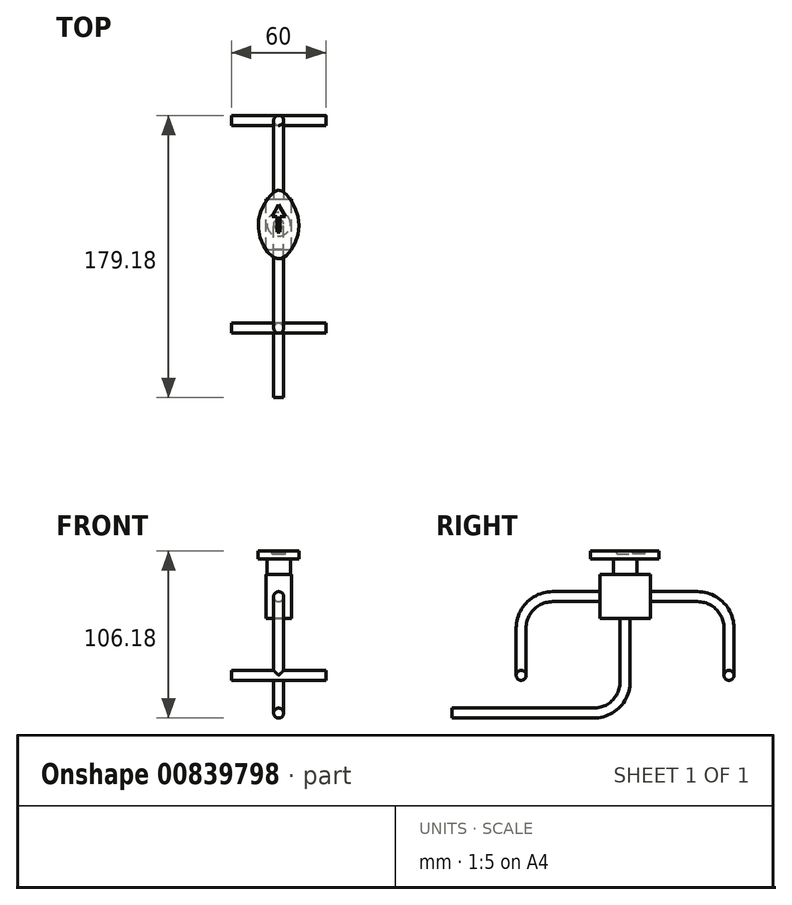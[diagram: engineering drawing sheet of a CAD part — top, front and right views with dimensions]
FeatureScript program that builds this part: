
annotation { "Feature Type Name" : "Feature", "Feature Type Description" : "" }
export const myFeature = defineFeature(function(context is Context, id is Id, definition is map)
    precondition{}
    {
        {
            var Q0;
            Q0=qCreatedBy(makeId("Front.planeOp"),FACE);
            var sketch = newSketch(context, id + "F0", { "sketchPlane" : qUnion([Q0])});
            skLineSegment(sketch, "E0.bottom", {"start": v(-64.04, 98.56) * mm, "end": v(-48.04, 98.56) * mm});
            skLineSegment(sketch, "E0.top", {"start": v(-64.04, 70.56) * mm, "end": v(-48.04, 70.56) * mm});
            skLineSegment(sketch, "E0.left", {"start": v(-64.04, 98.56) * mm, "end": v(-64.04, 70.56) * mm});
            skLineSegment(sketch, "E0.right", {"start": v(-48.04, 98.56) * mm, "end": v(-48.04, 70.56) * mm});
            skLineSegment(sketch, "E1", {"start": v(-56.04, 70.56) * mm, "end": v(-56.04, 30.56) * mm});
            skSolve(sketch);
        }
        {
            var Q0;
            Q0=makeQuery(id+"F0.imprint","IMPRINT",FACE,{"disambiguationData":[TD([[makeQuery(id+"F0.imprint","IMPRINT",EDGE,{"derivedFrom":sQuery(id+"F0.wireOp",EDGE,"E0.bottom")}),-1.0]])]});
            extrude(context, id + "F1", {"entities" : qUnion([Q0]), "endBound" : BoundingType.SYMMETRIC, "depth" : 32 * mm, "offsetDistance" : 25 * mm});
        }
        {
            var Q0;
            Q0=sQuery(id+"F0.wireOp",EDGE,"E1");
            cPlane(context, id + "F2", {"entities" : qUnion([Q0]), "cplaneType" : CPlaneType.LINE_ANGLE, "offset" : 25 * mm, "angle" : 0 * degree, "width" : 150 * mm, "height" : 150 * mm});
        }
        {
            var Q0;
            Q0=qCreatedBy(id+"F2.planeOp",FACE);
            var sketch = newSketch(context, id + "F3", { "sketchPlane" : qUnion([Q0])});
            skLineSegment(sketch, "E2", {"start": v(0, 30.56) * mm, "end": v(40, 30.56) * mm, "construction": true});
            skArc(sketch, "E3", {"start": v(0, 30.56) * mm, "mid": v(5.86, 16.41) * mm, "end": v(20, 10.56) * mm});
            skLineSegment(sketch, "E4", {"start": v(20, 10.56) * mm, "end": v(110, 10.56) * mm});
            skSolve(sketch);
        }
        {
            var Q0;
            Q0=sQuery(id+"F3.wireOp",VERTEX,"E4.end");
            var Q1;
            Q1=sQuery(id+"F3.wireOp",EDGE,"E4");
            cPlane(context, id + "F4", {"entities" : qUnion([Q0, Q1]), "cplaneType" : CPlaneType.CURVE_POINT, "offset" : 25 * mm, "width" : 150 * mm, "height" : 150 * mm});
        }
        {
            var Q0;
            Q0=qCreatedBy(id+"F4.planeOp",FACE);
            var sketch = newSketch(context, id + "F5", { "sketchPlane" : qUnion([Q0])});
            skCircle(sketch, "E5", {"center": v(-56.04, 10.56) * mm, "radius": 3.17 * mm});
            skSolve(sketch);
        }
        {
            var Q0;
            Q0=makeQuery(id+"F5.imprint","IMPRINT",FACE,{"disambiguationData":[TD([[makeQuery(id+"F5.imprint","IMPRINT",EDGE,{"derivedFrom":sQuery(id+"F5.wireOp",EDGE,"E5")}),1.0]])]});
            var Q1;
            Q1=sQuery(id+"F3.wireOp",EDGE,"E4");
            var Q2;
            Q2=sQuery(id+"F3.wireOp",EDGE,"E3");
            var Q3;
            Q3=sQuery(id+"F0.wireOp",EDGE,"E1");
            sweep(context, id + "F6", {"operationType" : NewBodyOperationType.ADD, "profiles" : qUnion([Q0]), "path" : qUnion([Q1, Q2, Q3])});
        }
        {
            var Q0;
            Q0=makeQuery(id+"F1.opExtrude","SWEPT_FACE",FACE,{"disambiguationData":[OSD([sQuery(id+"F0.wireOp",EDGE,"E0.bottom")])]});
            var sketch = newSketch(context, id + "F7", { "sketchPlane" : qUnion([Q0])});
            skLineSegment(sketch, "E6", {"start": v(-56.04, -16) * mm, "end": v(-56.04, 16) * mm, "construction": true});
            skCircle(sketch, "E7", {"center": v(-56.04, 0) * mm, "radius": 7.5 * mm});
            skSolve(sketch);
        }
        {
            var Q0;
            Q0 = qSketchRegion(id + "F7", true);
            extrude(context, id + "F8", {"entities" : qUnion([Q0]), "operationType" : NewBodyOperationType.ADD, "depth" : 10 * mm, "offsetDistance" : 25 * mm});
        }
        {
            var Q0;
            Q0=makeQuery(id+"F8.opExtrude","CAP_FACE",FACE,{"disambiguationData":[OSD([sQuery(id+"F7.wireOp",EDGE,"E7")])],"isStart":false});
            var sketch = newSketch(context, id + "F9", { "sketchPlane" : qUnion([Q0])});
            skLineSegment(sketch, "E8.bottom", {"start": v(-69.04, 20.5) * mm, "end": v(-43.04, 20.5) * mm, "construction": true});
            skLineSegment(sketch, "E8.top", {"start": v(-69.04, -20.5) * mm, "end": v(-43.04, -20.5) * mm, "construction": true});
            skLineSegment(sketch, "E8.left", {"start": v(-69.04, 20.5) * mm, "end": v(-69.04, -20.5) * mm, "construction": true});
            skLineSegment(sketch, "E8.right", {"start": v(-43.04, 20.5) * mm, "end": v(-43.04, -20.5) * mm, "construction": true});
            skPoint(sketch, "E8.middle", {"position": v(-56.04, 0) * mm});
            skFitSpline(sketch, "E9", {"points": [v(-59.04, 20.5) * mm, v(-69.04, 0) * mm, v(-60.04, -20.5) * mm, v(-52.04, -20.5) * mm, v(-43.04, 0) * mm, v(-53.04, 20.5) * mm, v(-59.04, 20.5) * mm]});
            skSolve(sketch);
        }
        {
            var Q0;
            Q0=makeQuery(id+"F9.imprint","IMPRINT",FACE,{"disambiguationData":[TD([[makeQuery(id+"F9.imprint","IMPRINT",EDGE,{"derivedFrom":sQuery(id+"F9.wireOp",EDGE,"E9")}),1.0]])]});
            var Q1;
            Q1=makeQuery(id+"F9.imprint","IMPRINT",FACE,{"disambiguationData":[TD([[makeQuery(id+"F9.imprint","IMPRINT",EDGE,{"derivedFrom":makeQuery(id+"F8.opExtrude","CAP_EDGE",EDGE,{"disambiguationData":[OSD([sQuery(id+"F7.wireOp",EDGE,"E7")])],"isStart":false})}),1.0]])]});
            extrude(context, id + "F10", {"entities" : qUnion([Q0, Q1]), "operationType" : NewBodyOperationType.ADD, "depth" : 5 * mm, "offsetDistance" : 25 * mm});
        }
        {
            var Q0;
            Q0=makeQuery(id+"F1.opExtrude","CAP_FACE",FACE,{"disambiguationData":[OSD([sQuery(id+"F0.wireOp",EDGE,"E0.bottom"),sQuery(id+"F0.wireOp",EDGE,"E0.top"),sQuery(id+"F0.wireOp",EDGE,"E0.left"),sQuery(id+"F0.wireOp",EDGE,"E0.right")])],"isStart":false});
            var sketch = newSketch(context, id + "F11", { "sketchPlane" : qUnion([Q0])});
            skLineSegment(sketch, "E10", {"start": v(-56.04, 70.56) * mm, "end": v(-56.04, 98.56) * mm, "construction": true});
            skSolve(sketch);
        }
        {
            var Q0;
            Q0=sQuery(id+"F11.wireOp",EDGE,"E10");
            cPlane(context, id + "F12", {"entities" : qUnion([Q0]), "cplaneType" : CPlaneType.LINE_ANGLE, "offset" : 25 * mm, "angle" : 0 * degree, "width" : 150 * mm, "height" : 150 * mm});
        }
        {
            var Q0;
            Q0=qCreatedBy(id+"F12.planeOp",FACE);
            var sketch = newSketch(context, id + "F13", { "sketchPlane" : qUnion([Q0])});
            skLineSegment(sketch, "E11", {"start": v(-16, 84.56) * mm, "end": v(-46, 84.56) * mm});
            skLineSegment(sketch, "E12", {"start": v(-46, 84.56) * mm, "end": v(-46, 44.56) * mm, "construction": true});
            skArc(sketch, "E13", {"start": v(-46, 84.56) * mm, "mid": v(-60.14, 78.7) * mm, "end": v(-66, 64.56) * mm});
            skLineSegment(sketch, "E14", {"start": v(-66, 64.56) * mm, "end": v(-66, 34.56) * mm});
            skSolve(sketch);
        }
        {
            var Q0;
            Q0=sQuery(id+"F13.wireOp",EDGE,"E14");
            cPlane(context, id + "F14", {"entities" : qUnion([Q0]), "cplaneType" : CPlaneType.LINE_ANGLE, "offset" : 25 * mm, "angle" : 270 * degree, "width" : 150 * mm, "height" : 150 * mm});
        }
        {
            var Q0;
            Q0=qCreatedBy(id+"F14.planeOp",FACE);
            var sketch = newSketch(context, id + "F15", { "sketchPlane" : qUnion([Q0])});
            skPoint(sketch, "E15", {"position": v(-56.04, 34.56) * mm});
            skLineSegment(sketch, "E16", {"start": v(-56.04, 34.56) * mm, "end": v(-26.04, 34.56) * mm});
            skSolve(sketch);
        }
        {
            var Q0;
            Q0=sQuery(id+"F15.wireOp",VERTEX,"E16.end");
            var Q1;
            Q1=sQuery(id+"F15.wireOp",EDGE,"E16");
            cPlane(context, id + "F16", {"entities" : qUnion([Q0, Q1]), "cplaneType" : CPlaneType.CURVE_POINT, "offset" : 25 * mm, "width" : 150 * mm, "height" : 150 * mm});
        }
        {
            var Q0;
            Q0=qCreatedBy(id+"F16.planeOp",FACE);
            var sketch = newSketch(context, id + "F17", { "sketchPlane" : qUnion([Q0])});
            skCircle(sketch, "E17", {"center": v(-66, 34.56) * mm, "radius": 3.17 * mm});
            skSolve(sketch);
        }
        {
            var Q0;
            Q0=makeQuery(id+"F17.imprint","IMPRINT",FACE,{"disambiguationData":[TD([[makeQuery(id+"F17.imprint","IMPRINT",EDGE,{"derivedFrom":sQuery(id+"F17.wireOp",EDGE,"E17")}),1.0]])]});
            var Q1;
            Q1=sQuery(id+"F15.wireOp",EDGE,"E16");
            var Q2;
            Q2=sQuery(id+"F13.wireOp",EDGE,"E14");
            var Q3;
            Q3=sQuery(id+"F13.wireOp",EDGE,"E13");
            var Q4;
            Q4=sQuery(id+"F13.wireOp",EDGE,"E11");
            sweep(context, id + "F18", {"operationType" : NewBodyOperationType.ADD, "profiles" : qUnion([Q0]), "path" : qUnion([Q1, Q2, Q3, Q4])});
        }
        {
            var Q0;
            Q0=qCreatedBy(id+"F14.planeOp",FACE);
            var sketch = newSketch(context, id + "F19", { "sketchPlane" : qUnion([Q0])});
            skLineSegment(sketch, "E18", {"start": v(-86.04, 34.56) * mm, "end": v(-56.04, 34.56) * mm});
            skSolve(sketch);
        }
        {
            var Q0;
            Q0=sQuery(id+"F19.wireOp",VERTEX,"E18.start");
            var Q1;
            Q1=sQuery(id+"F19.wireOp",EDGE,"E18");
            cPlane(context, id + "F20", {"entities" : qUnion([Q0, Q1]), "cplaneType" : CPlaneType.CURVE_POINT, "offset" : 25 * mm, "width" : 150 * mm, "height" : 150 * mm});
        }
        {
            var Q0;
            Q0=qCreatedBy(id+"F20.planeOp",FACE);
            var sketch = newSketch(context, id + "F21", { "sketchPlane" : qUnion([Q0])});
            skCircle(sketch, "E19", {"center": v(-66, 34.56) * mm, "radius": 3.17 * mm});
            skSolve(sketch);
        }
        {
            var Q0;
            Q0=makeQuery(id+"F21.imprint","IMPRINT",FACE,{"disambiguationData":[TD([[makeQuery(id+"F21.imprint","IMPRINT",EDGE,{"derivedFrom":sQuery(id+"F21.wireOp",EDGE,"E19")}),1.0]])]});
            var Q1;
            Q1=sQuery(id+"F19.wireOp",EDGE,"E18");
            sweep(context, id + "F22", {"operationType" : NewBodyOperationType.ADD, "profiles" : qUnion([Q0]), "path" : qUnion([Q1])});
        }
        {
            var Q0;
            Q0=qCreatedBy(id+"F12.planeOp",FACE);
            var sketch = newSketch(context, id + "F23", { "sketchPlane" : qUnion([Q0])});
            skLineSegment(sketch, "E20", {"start": v(16, 84.56) * mm, "end": v(46, 84.56) * mm});
            skLineSegment(sketch, "E21", {"start": v(46, 84.56) * mm, "end": v(46, 64.56) * mm, "construction": true});
            skArc(sketch, "E22", {"start": v(46, 84.56) * mm, "mid": v(60.14, 78.7) * mm, "end": v(66, 64.56) * mm});
            skLineSegment(sketch, "E23", {"start": v(66, 64.56) * mm, "end": v(66, 34.56) * mm});
            skSolve(sketch);
        }
        {
            var Q0;
            Q0=sQuery(id+"F23.wireOp",VERTEX,"E23.end");
            var Q1;
            Q1=sQuery(id+"F23.wireOp",EDGE,"E23");
            cPlane(context, id + "F24", {"entities" : qUnion([Q0, Q1]), "cplaneType" : CPlaneType.CURVE_POINT, "offset" : 25 * mm, "width" : 150 * mm, "height" : 150 * mm});
        }
        {
            var Q0;
            Q0=qCreatedBy(id+"F24.planeOp",FACE);
            var sketch = newSketch(context, id + "F25", { "sketchPlane" : qUnion([Q0])});
            skLineSegment(sketch, "E24", {"start": v(-56.04, -66) * mm, "end": v(-86.04, -66) * mm});
            skLineSegment(sketch, "E25", {"start": v(-56.04, -66) * mm, "end": v(-26.04, -66) * mm});
            skSolve(sketch);
        }
        {
            var Q0;
            Q0=sQuery(id+"F25.wireOp",VERTEX,"E25.end");
            var Q1;
            Q1=sQuery(id+"F25.wireOp",EDGE,"E25");
            cPlane(context, id + "F26", {"entities" : qUnion([Q0, Q1]), "cplaneType" : CPlaneType.CURVE_POINT, "offset" : 25 * mm, "width" : 150 * mm, "height" : 150 * mm});
        }
        {
            var Q0;
            Q0=qCreatedBy(id+"F26.planeOp",FACE);
            var sketch = newSketch(context, id + "F27", { "sketchPlane" : qUnion([Q0])});
            skCircle(sketch, "E26", {"center": v(66, 34.56) * mm, "radius": 3.17 * mm});
            skSolve(sketch);
        }
        {
            var Q0;
            Q0=makeQuery(id+"F27.imprint","IMPRINT",FACE,{"disambiguationData":[TD([[makeQuery(id+"F27.imprint","IMPRINT",EDGE,{"derivedFrom":sQuery(id+"F27.wireOp",EDGE,"E26")}),1.0]])]});
            var Q1;
            Q1=sQuery(id+"F25.wireOp",EDGE,"E25");
            var Q2;
            Q2=sQuery(id+"F23.wireOp",EDGE,"E23");
            var Q3;
            Q3=sQuery(id+"F23.wireOp",EDGE,"E22");
            var Q4;
            Q4=sQuery(id+"F23.wireOp",EDGE,"E20");
            sweep(context, id + "F28", {"operationType" : NewBodyOperationType.ADD, "profiles" : qUnion([Q0]), "path" : qUnion([Q1, Q2, Q3, Q4])});
        }
        {
            var Q0;
            Q0=sQuery(id+"F25.wireOp",EDGE,"E24");
            var Q1;
            Q1=sQuery(id+"F25.wireOp",VERTEX,"E24.end");
            cPlane(context, id + "F29", {"entities" : qUnion([Q0, Q1]), "cplaneType" : CPlaneType.CURVE_POINT, "offset" : 25 * mm, "width" : 150 * mm, "height" : 150 * mm});
        }
        {
            var Q0;
            Q0=qCreatedBy(id+"F29.planeOp",FACE);
            var sketch = newSketch(context, id + "F30", { "sketchPlane" : qUnion([Q0])});
            skCircle(sketch, "E27", {"center": v(-66, 34.56) * mm, "radius": 3.17 * mm});
            skSolve(sketch);
        }
        {
            var Q0;
            Q0=makeQuery(id+"F30.imprint","IMPRINT",FACE,{"disambiguationData":[TD([[makeQuery(id+"F30.imprint","IMPRINT",EDGE,{"derivedFrom":sQuery(id+"F30.wireOp",EDGE,"E27")}),1.0]])]});
            var Q1;
            Q1=sQuery(id+"F25.wireOp",EDGE,"E24");
            sweep(context, id + "F31", {"operationType" : NewBodyOperationType.ADD, "profiles" : qUnion([Q0]), "path" : qUnion([Q1])});
        }
        {
            var Q0;
            Q0=makeQuery(id+"F10.opExtrude","CAP_FACE",FACE,{"disambiguationData":[OSD([sQuery(id+"F9.wireOp",EDGE,"E9")])],"isStart":false});
            var sketch = newSketch(context, id + "F32", { "sketchPlane" : qUnion([Q0])});
            skLineSegment(sketch, "E28.bottom", {"start": v(-57.04, -5) * mm, "end": v(-55.04, -5) * mm});
            skLineSegment(sketch, "E28.top", {"start": v(-57.04, 5) * mm, "end": v(-55.04, 5) * mm, "construction": true});
            skLineSegment(sketch, "E28.left", {"start": v(-57.04, -5) * mm, "end": v(-57.04, 5) * mm});
            skLineSegment(sketch, "E28.right", {"start": v(-55.04, -5) * mm, "end": v(-55.04, 5) * mm});
            skPoint(sketch, "E28.middle", {"position": v(-56.04, 0) * mm});
            skLineSegment(sketch, "E29", {"start": v(-69.04, 0) * mm, "end": v(-43.04, 0) * mm, "construction": true});
            skLineSegment(sketch, "E30", {"start": v(-56.04, 0) * mm, "end": v(-56.04, 15) * mm, "construction": true});
            skPoint(sketch, "E31", {"position": v(-56.04, 7.5) * mm});
            skCircle(sketch, "E32.cCircle", {"center": v(-56.04, 7.5) * mm, "radius": 5 * mm, "construction": true});
            skLineSegment(sketch, "E32.0", {"start": v(-56.04, 12.5) * mm, "end": v(-51.71, 5) * mm});
            skLineSegment(sketch, "E32.1", {"start": v(-51.71, 5) * mm, "end": v(-60.37, 5) * mm});
            skLineSegment(sketch, "E32.2", {"start": v(-60.37, 5) * mm, "end": v(-56.04, 12.5) * mm});
            skSolve(sketch);
        }
        {
            var Q0;
            Q0 = qSketchRegion(id + "F32", true);
            extrude(context, id + "F33", {"entities" : qUnion([Q0]), "operationType" : NewBodyOperationType.REMOVE, "oppositeDirection" : true, "depth" : 2 * mm, "offsetDistance" : 25 * mm});
        }
    });
